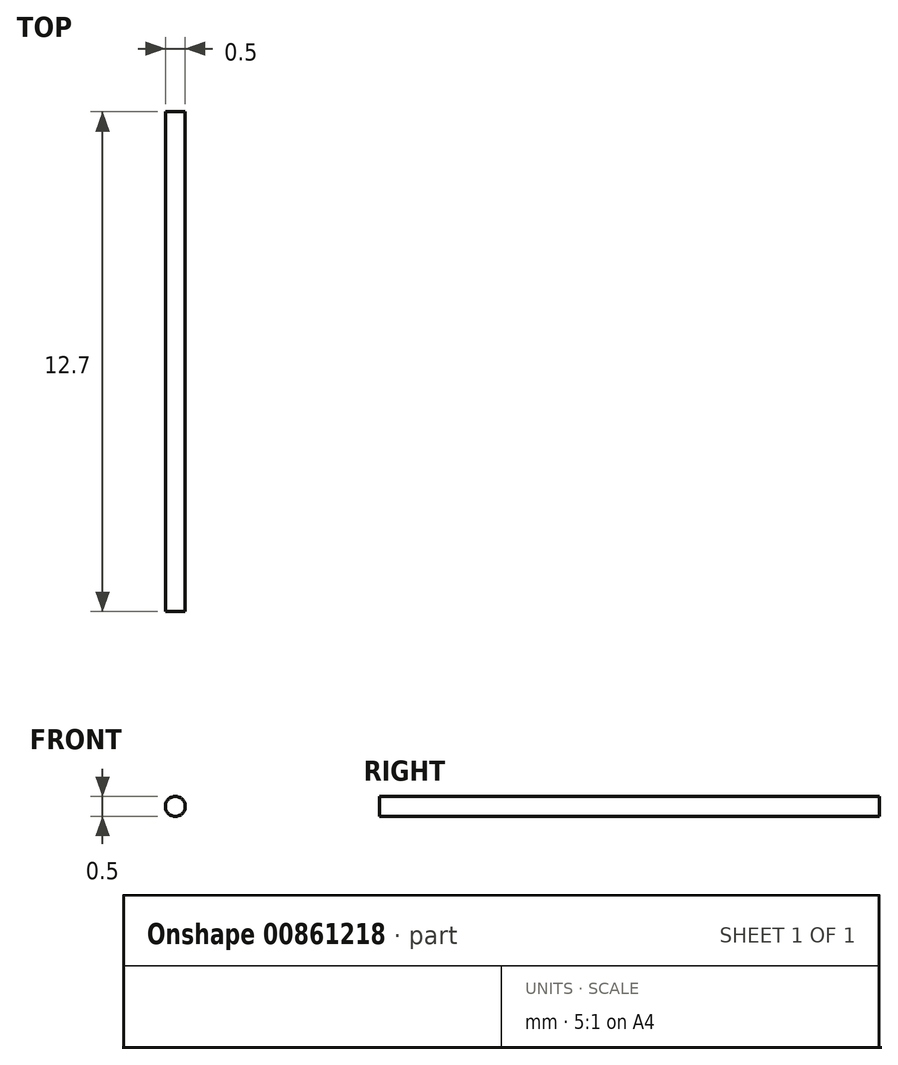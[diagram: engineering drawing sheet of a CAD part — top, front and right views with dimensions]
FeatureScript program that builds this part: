
annotation { "Feature Type Name" : "Feature", "Feature Type Description" : "" }
export const myFeature = defineFeature(function(context is Context, id is Id, definition is map)
    precondition{}
    {
        {
            var Q0;
            Q0=qCreatedBy(makeId("Front.planeOp"),FACE);
            var sketch = newSketch(context, id + "F0", { "sketchPlane" : qUnion([Q0])});
            skCircle(sketch, "E0", {"center": v(0, 0) * mm, "radius": 0.25 * mm});
            skSolve(sketch);
        }
        {
            var Q0;
            Q0=makeQuery(id+"F0.imprint","IMPRINT",FACE,{"disambiguationData":[TD([[makeQuery(id+"F0.imprint","IMPRINT",EDGE,{"derivedFrom":sQuery(id+"F0.wireOp",EDGE,"E0")}),1.0]])]});
            extrude(context, id + "F1", {"entities" : qUnion([Q0]), "depth" : 12.7 * mm, "offsetDistance" : 25.4 * mm});
        }
    });
